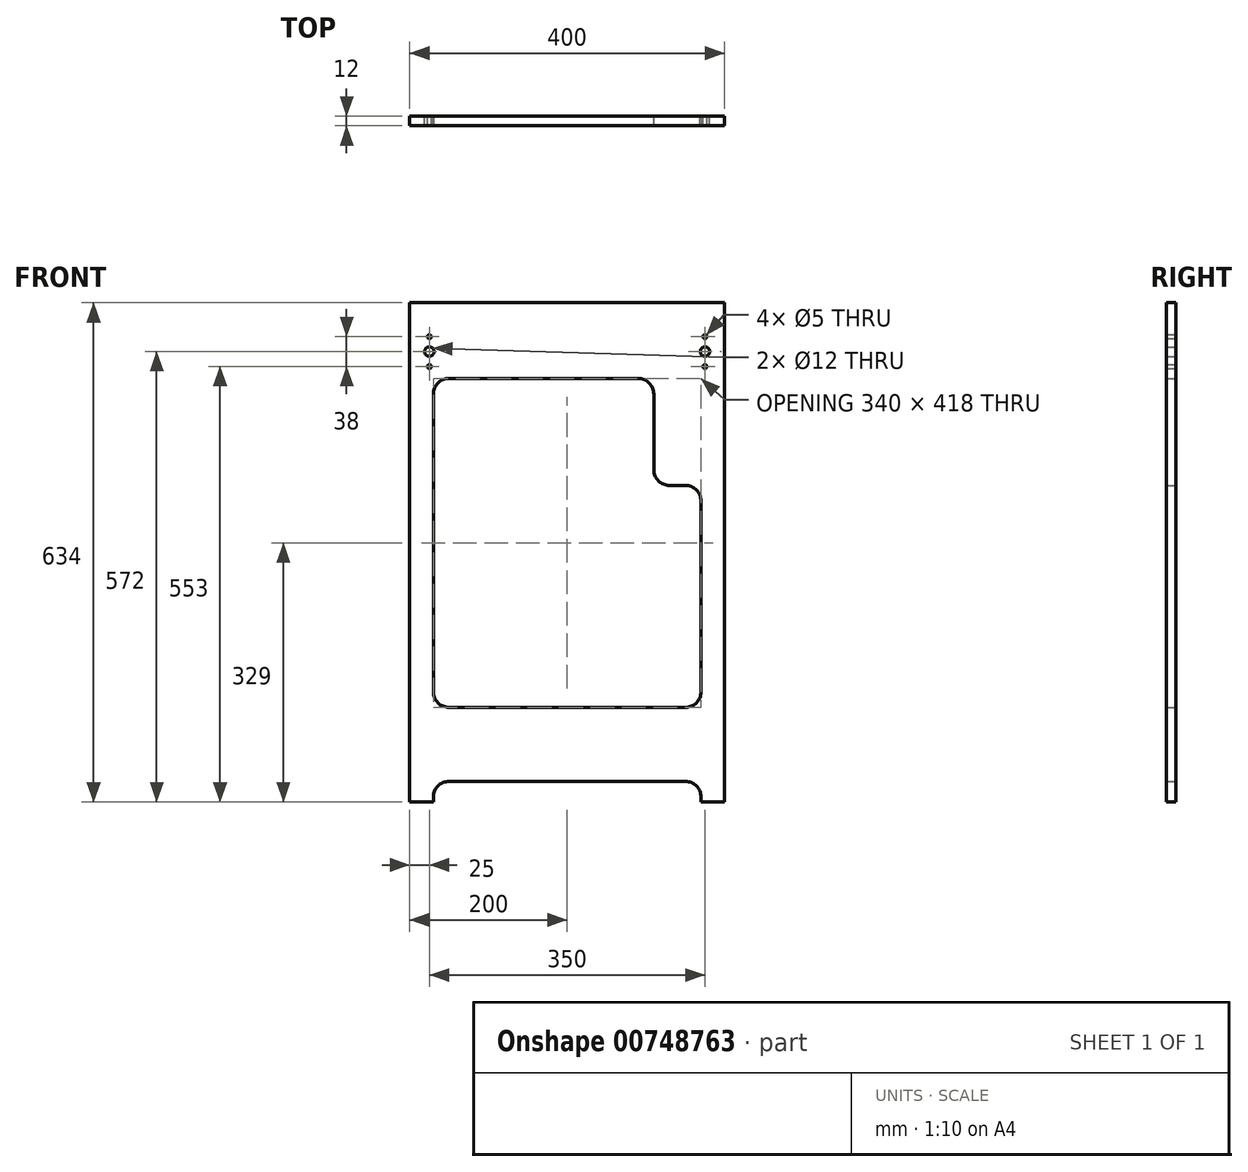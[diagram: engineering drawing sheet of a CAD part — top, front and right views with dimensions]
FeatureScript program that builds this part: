
annotation { "Feature Type Name" : "Feature", "Feature Type Description" : "" }
export const myFeature = defineFeature(function(context is Context, id is Id, definition is map)
    precondition{}
    {
        {
            assignVariable(context, id + "F0", {"name" : "Width", "anyValue" : 12});
        }
        {
            var Q0;
            Q0=qCreatedBy(makeId("Front.planeOp"),FACE);
            var sketch = newSketch(context, id + "F1", { "sketchPlane" : qUnion([Q0])});
            skLineSegment(sketch, "E0.bottom", {"start": v(90, 278) * mm, "end": v(-150, 278) * mm});
            skLineSegment(sketch, "E0.top", {"start": v(150, -140) * mm, "end": v(-150, -140) * mm});
            skLineSegment(sketch, "E0.left", {"start": v(170, 122) * mm, "end": v(170, -120) * mm});
            skLineSegment(sketch, "E0.right", {"start": v(-170, 258) * mm, "end": v(-170, -120) * mm});
            skLineSegment(sketch, "E1.bottom", {"start": v(200, 374) * mm, "end": v(-200, 374) * mm});
            skLineSegment(sketch, "E1.top", {"start": v(200, -260) * mm, "end": v(-200, -260) * mm});
            skLineSegment(sketch, "E1.left", {"start": v(200, 374) * mm, "end": v(200, -260) * mm});
            skLineSegment(sketch, "E1.right", {"start": v(-200, 374) * mm, "end": v(-200, -260) * mm});
            skLineSegment(sketch, "E2", {"start": v(-200, -222) * mm, "end": v(200, -222) * mm});
            skLineSegment(sketch, "E3", {"start": v(-200, -162) * mm, "end": v(200, -162) * mm});
            skLineSegment(sketch, "E4", {"start": v(-200, -150) * mm, "end": v(200, -150) * mm});
            skLineSegment(sketch, "E5", {"start": v(-170, -254) * mm, "end": v(-170, -260) * mm});
            skLineSegment(sketch, "E6", {"start": v(170, -254) * mm, "end": v(170, -260) * mm});
            skLineSegment(sketch, "E7", {"start": v(-150, -234) * mm, "end": v(150, -234) * mm});
            skArc(sketch, "E8.filletArc", {"start": v(-150, -234) * mm, "mid": v(-164.14, -239.86) * mm, "end": v(-170, -254) * mm});
            skArc(sketch, "E9.filletArc", {"start": v(170, -254) * mm, "mid": v(164.14, -239.86) * mm, "end": v(150, -234) * mm});
            skLineSegment(sketch, "E10", {"start": v(-150, -234) * mm, "end": v(-200, -234) * mm});
            skLineSegment(sketch, "E11", {"start": v(150, -234) * mm, "end": v(200, -234) * mm});
            skCircle(sketch, "E12", {"center": v(-175, 312) * mm, "radius": 6 * mm});
            skCircle(sketch, "E13", {"center": v(175, 312) * mm, "radius": 6 * mm});
            skCircle(sketch, "E14", {"center": v(175, 331) * mm, "radius": 2.5 * mm});
            skCircle(sketch, "E15", {"center": v(175, 293) * mm, "radius": 2.5 * mm});
            skCircle(sketch, "E16", {"center": v(-175, 331) * mm, "radius": 2.5 * mm});
            skCircle(sketch, "E17", {"center": v(-175, 293) * mm, "radius": 2.5 * mm});
            skPoint(sketch, "E18.visualSharp", {"position": v(-170, 278) * mm});
            skArc(sketch, "E18.filletArc", {"start": v(-150, 278) * mm, "mid": v(-164.14, 272.14) * mm, "end": v(-170, 258) * mm});
            skPoint(sketch, "E19.visualSharp", {"position": v(170, -140) * mm});
            skArc(sketch, "E19.filletArc", {"start": v(150, -140) * mm, "mid": v(164.14, -134.14) * mm, "end": v(170, -120) * mm});
            skPoint(sketch, "E20.visualSharp", {"position": v(-170, -140) * mm});
            skArc(sketch, "E20.filletArc", {"start": v(-170, -120) * mm, "mid": v(-164.14, -134.14) * mm, "end": v(-150, -140) * mm});
            skPoint(sketch, "E21.middle", {"position": v(175, 202) * mm});
            skLineSegment(sketch, "E22", {"start": v(150, 142) * mm, "end": v(130, 142) * mm});
            skLineSegment(sketch, "E23", {"start": v(110, 162) * mm, "end": v(110, 258) * mm});
            skArc(sketch, "E24.filletArc", {"start": v(110, 258) * mm, "mid": v(104.14, 272.14) * mm, "end": v(90, 278) * mm});
            skPoint(sketch, "E25.visualSharp", {"position": v(110, 142) * mm});
            skArc(sketch, "E25.filletArc", {"start": v(110, 162) * mm, "mid": v(115.86, 147.86) * mm, "end": v(130, 142) * mm});
            skPoint(sketch, "E26.newPointA", {"position": v(170, 142) * mm});
            skArc(sketch, "E26.filletArc", {"start": v(170, 122) * mm, "mid": v(164.14, 136.14) * mm, "end": v(150, 142) * mm});
            skSolve(sketch);
        }
        {
            var Q0;
            Q0=makeQuery(id+"F1.imprint","IMPRINT",FACE,{"disambiguationData":[TD([[makeQuery(id+"F1.imprint","IMPRINT",EDGE,{"derivedFrom":sQuery(id+"F1.wireOp",EDGE,"E0.bottom")}),-1.0]])]});
            var Q1;
            {var subQ0=sQuery(id+"F1.wireOp",EDGE,"E3");Q1=makeQuery(id+"F1.imprint","IMPRINT",FACE,{"disambiguationData":[TD([[makeQuery(id+"F1.imprint","IMPRINT",EDGE,{"derivedFrom":subQ0}),1.0]])]});}
            var Q2;
            {var subQ0=sQuery(id+"F1.wireOp",EDGE,"E2");Q2=makeQuery(id+"F1.imprint","IMPRINT",FACE,{"disambiguationData":[TD([[makeQuery(id+"F1.imprint","IMPRINT",EDGE,{"derivedFrom":subQ0}),1.0]])]});}
            var Q3;
            {var subQ0=sQuery(id+"F1.wireOp",EDGE,"E2");Q3=makeQuery(id+"F1.imprint","IMPRINT",FACE,{"disambiguationData":[TD([[makeQuery(id+"F1.imprint","IMPRINT",EDGE,{"derivedFrom":subQ0}),-1.0]])]});}
            var Q4;
            {var subQ0=sQuery(id+"F1.wireOp",EDGE,"E6");Q4=makeQuery(id+"F1.imprint","IMPRINT",FACE,{"disambiguationData":[TD([[makeQuery(id+"F1.imprint","IMPRINT",EDGE,{"derivedFrom":subQ0}),1.0]])]});}
            var Q5;
            {var subQ4=sQuery(id+"F1.wireOp",EDGE,"E5");Q5=makeQuery(id+"F1.imprint","IMPRINT",FACE,{"disambiguationData":[TD([[makeQuery(id+"F1.imprint","IMPRINT",EDGE,{"derivedFrom":subQ4}),-1.0]])]});}
            extrude(context, id + "F2", {"entities" : qUnion([Q0, Q1, Q2, Q3, Q4, Q5]), "depth" : (getVariable(context, 'Width')) * mm, "offsetDistance" : 25 * mm});
        }
    });
